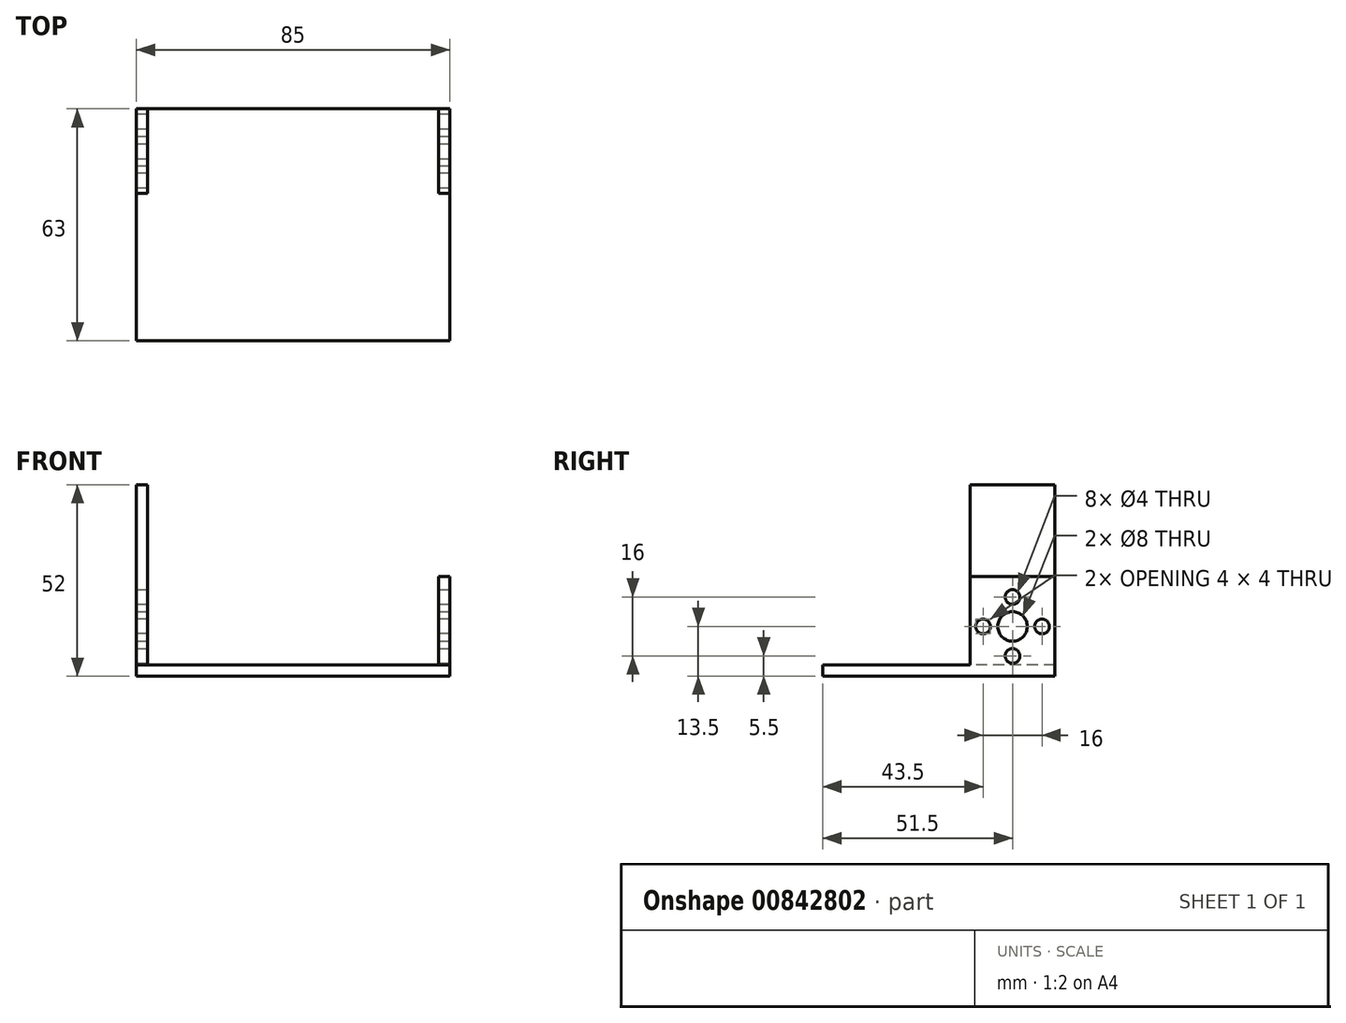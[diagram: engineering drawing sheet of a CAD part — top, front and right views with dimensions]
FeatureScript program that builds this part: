
annotation { "Feature Type Name" : "Feature", "Feature Type Description" : "" }
export const myFeature = defineFeature(function(context is Context, id is Id, definition is map)
    precondition{}
    {
        {
            var Q0;
            Q0=qCreatedBy(makeId("Top.planeOp"),FACE);
            var sketch = newSketch(context, id + "F0", { "sketchPlane" : qUnion([Q0])});
            skLineSegment(sketch, "E0.bottom", {"start": v(0, 0) * mm, "end": v(85, 0) * mm});
            skLineSegment(sketch, "E0.top", {"start": v(0, 23) * mm, "end": v(85, 23) * mm});
            skLineSegment(sketch, "E0.left", {"start": v(0, 0) * mm, "end": v(0, 23) * mm});
            skLineSegment(sketch, "E0.right", {"start": v(85, 0) * mm, "end": v(85, 23) * mm});
            skLineSegment(sketch, "E1.top", {"start": v(0, -40) * mm, "end": v(85, -40) * mm});
            skLineSegment(sketch, "E1.left", {"start": v(0, 0) * mm, "end": v(0, -40) * mm});
            skLineSegment(sketch, "E1.right", {"start": v(85, 0) * mm, "end": v(85, -40) * mm});
            skSolve(sketch);
        }
        {
            var Q0;
            Q0=qSketchRegion(id+"F0",true);
            extrude(context, id + "F1", {"entities" : qUnion([Q0]), "depth" : 3 * mm, "offsetDistance" : 25 * mm});
        }
        {
            var Q0;
            Q0=makeQuery(id+"F1.opExtrude","CAP_FACE",FACE,{"disambiguationData":[OSD([sQuery(id+"F0.wireOp",EDGE,"E0.bottom"),sQuery(id+"F0.wireOp",EDGE,"E0.top"),sQuery(id+"F0.wireOp",EDGE,"E0.left"),sQuery(id+"F0.wireOp",EDGE,"E0.right")])],"isStart":false});
            var sketch = newSketch(context, id + "F2", { "sketchPlane" : qUnion([Q0])});
            skLineSegment(sketch, "E2.bottom", {"start": v(0, 23) * mm, "end": v(3, 23) * mm});
            skLineSegment(sketch, "E2.top", {"start": v(0, 0) * mm, "end": v(3, 0) * mm});
            skLineSegment(sketch, "E2.left", {"start": v(0, 23) * mm, "end": v(0, 0) * mm});
            skLineSegment(sketch, "E2.right", {"start": v(3, 23) * mm, "end": v(3, 0) * mm});
            skLineSegment(sketch, "E3.bottom", {"start": v(85, 23) * mm, "end": v(82, 23) * mm});
            skLineSegment(sketch, "E3.top", {"start": v(85, 0) * mm, "end": v(82, 0) * mm});
            skLineSegment(sketch, "E3.left", {"start": v(85, 23) * mm, "end": v(85, 0) * mm});
            skLineSegment(sketch, "E3.right", {"start": v(82, 23) * mm, "end": v(82, 0) * mm});
            skSolve(sketch);
        }
        {
            var Q0;
            Q0=qSketchRegion(id+"F2",true);
            extrude(context, id + "F3", {"entities" : qUnion([Q0]), "operationType" : NewBodyOperationType.ADD, "depth" : 24 * mm, "offsetDistance" : 25 * mm});
        }
        {
            var Q0;
            Q0=makeQuery(id+"F3.opExtrude","CAP_FACE",FACE,{"disambiguationData":[OSD([sQuery(id+"F2.wireOp",EDGE,"E2.bottom"),sQuery(id+"F2.wireOp",EDGE,"E2.top"),sQuery(id+"F2.wireOp",EDGE,"E2.left"),sQuery(id+"F2.wireOp",EDGE,"E2.right")])],"isStart":false});
            var sketch = newSketch(context, id + "F4", { "sketchPlane" : qUnion([Q0])});
            skLineSegment(sketch, "E4.bottom", {"start": v(0, 23) * mm, "end": v(3, 23) * mm});
            skLineSegment(sketch, "E4.top", {"start": v(0, 0) * mm, "end": v(3, 0) * mm});
            skLineSegment(sketch, "E4.left", {"start": v(0, 23) * mm, "end": v(0, 0) * mm});
            skLineSegment(sketch, "E4.right", {"start": v(3, 23) * mm, "end": v(3, 0) * mm});
            skSolve(sketch);
        }
        {
            var Q0;
            Q0=qSketchRegion(id+"F4",true);
            extrude(context, id + "F5", {"entities" : qUnion([Q0]), "operationType" : NewBodyOperationType.ADD, "depth" : 25 * mm, "offsetDistance" : 25 * mm});
        }
        {
            var Q0;
            Q0=makeQuery(id+"F3.boolean.opBoolean","MERGE",FACE,{"derivedFrom":[makeQuery(id+"F1.opExtrude","SWEPT_FACE",FACE,{"disambiguationData":[OSD([sQuery(id+"F0.wireOp",EDGE,"E0.right"),sQuery(id+"F0.wireOp",EDGE,"E1.right")])]}),makeQuery(id+"F3.opExtrude","SWEPT_FACE",FACE,{"disambiguationData":[OSD([sQuery(id+"F2.wireOp",EDGE,"E3.left")])]})]});
            var sketch = newSketch(context, id + "F6", { "sketchPlane" : qUnion([Q0])});
            skLineSegment(sketch, "E5", {"start": v(0, 27) * mm, "end": v(23, 0) * mm, "construction": true});
            skLineSegment(sketch, "E6", {"start": v(23, 0) * mm, "end": v(23, 27) * mm, "construction": true});
            skLineSegment(sketch, "E7", {"start": v(23, 27) * mm, "end": v(0, 0) * mm, "construction": true});
            skCircle(sketch, "E8", {"center": v(11.5, 13.5) * mm, "radius": 4 * mm});
            skSolve(sketch);
        }
        {
            var Q0;
            Q0=qSketchRegion(id+"F6",true);
            extrude(context, id + "F7", {"entities" : qUnion([Q0]), "operationType" : NewBodyOperationType.REMOVE, "oppositeDirection" : true, "depth" : 200 * mm, "offsetDistance" : 25 * mm});
        }
        {
            var Q0;
            Q0=makeQuery(id+"F5.boolean.opBoolean","MERGE",FACE,{"derivedFrom":[makeQuery(id+"F3.boolean.opBoolean","MERGE",FACE,{"derivedFrom":[makeQuery(id+"F1.opExtrude","SWEPT_FACE",FACE,{"disambiguationData":[OSD([sQuery(id+"F0.wireOp",EDGE,"E0.left"),sQuery(id+"F0.wireOp",EDGE,"E1.left")])]}),makeQuery(id+"F3.opExtrude","SWEPT_FACE",FACE,{"disambiguationData":[OSD([sQuery(id+"F2.wireOp",EDGE,"E2.left")])]})]}),makeQuery(id+"F5.opExtrude","SWEPT_FACE",FACE,{"disambiguationData":[OSD([sQuery(id+"F4.wireOp",EDGE,"E4.left")])]})]});
            var sketch = newSketch(context, id + "F8", { "sketchPlane" : qUnion([Q0])});
            skLineSegment(sketch, "E9", {"start": v(-11.5, 13.5) * mm, "end": v(-19.5, 13.5) * mm});
            skLineSegment(sketch, "E10", {"start": v(-19.5, 13.5) * mm, "end": v(-11.5, 13.5) * mm});
            skLineSegment(sketch, "E11", {"start": v(-11.5, 13.5) * mm, "end": v(-3.5, 13.5) * mm});
            skCircle(sketch, "E12", {"center": v(-19.5, 13.5) * mm, "radius": 2 * mm});
            skCircle(sketch, "E13", {"center": v(-3.5, 13.5) * mm, "radius": 2 * mm});
            skSolve(sketch);
        }
        {
            var Q0;
            Q0=makeQuery(id+"F8.imprint","IMPRINT",FACE,{"disambiguationData":[TD([[makeQuery(id+"F8.imprint","IMPRINT",EDGE,{"derivedFrom":sQuery(id+"F8.wireOp",EDGE,"E13")}),1.0]])]});
            var Q1;
            Q1=makeQuery(id+"F8.imprint","IMPRINT",FACE,{"disambiguationData":[TD([[makeQuery(id+"F8.imprint","IMPRINT",EDGE,{"derivedFrom":sQuery(id+"F8.wireOp",EDGE,"E12")}),1.0]])]});
            var Q2;
            Q2=sQuery(id+"F8.wireOp",EDGE,"E13");
            var Q3;
            Q3=sQuery(id+"F8.wireOp",EDGE,"E12");
            extrude(context, id + "F9", {"entities" : qUnion([Q0, Q1]), "operationType" : NewBodyOperationType.REMOVE, "surfaceEntities" : qUnion([Q2, Q3]), "oppositeDirection" : true, "depth" : 250 * mm, "offsetDistance" : 25 * mm});
        }
        {
            var Q0;
            Q0=makeQuery(id+"F3.boolean.opBoolean","MERGE",FACE,{"derivedFrom":[makeQuery(id+"F1.opExtrude","SWEPT_FACE",FACE,{"disambiguationData":[OSD([sQuery(id+"F0.wireOp",EDGE,"E0.right"),sQuery(id+"F0.wireOp",EDGE,"E1.right")])]}),makeQuery(id+"F3.opExtrude","SWEPT_FACE",FACE,{"disambiguationData":[OSD([sQuery(id+"F2.wireOp",EDGE,"E3.left")])]})]});
            var sketch = newSketch(context, id + "F10", { "sketchPlane" : qUnion([Q0])});
            skLineSegment(sketch, "E14", {"start": v(11.5, 13.5) * mm, "end": v(11.5, 21.5) * mm});
            skLineSegment(sketch, "E15", {"start": v(11.5, 21.5) * mm, "end": v(11.5, 13.5) * mm});
            skLineSegment(sketch, "E16", {"start": v(11.5, 5.5) * mm, "end": v(11.5, 13.5) * mm});
            skCircle(sketch, "E17", {"center": v(11.5, 21.5) * mm, "radius": 2 * mm});
            skCircle(sketch, "E18", {"center": v(11.5, 5.5) * mm, "radius": 2 * mm});
            skSolve(sketch);
        }
        {
            var Q0;
            Q0 = qSketchRegion(id + "F10", true);
            extrude(context, id + "F11", {"entities" : qUnion([Q0]), "operationType" : NewBodyOperationType.REMOVE, "oppositeDirection" : true, "depth" : 250 * mm, "offsetDistance" : 25 * mm});
        }
    });
